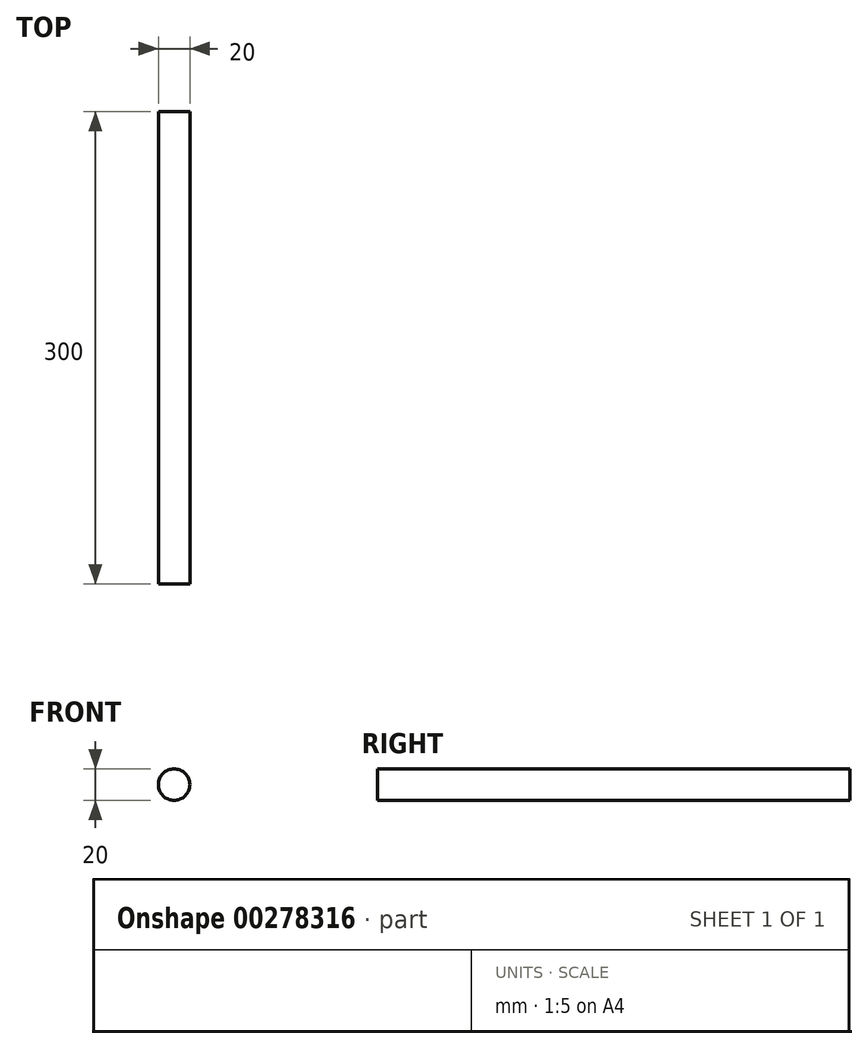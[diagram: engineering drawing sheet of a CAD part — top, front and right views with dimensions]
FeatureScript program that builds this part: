
annotation { "Feature Type Name" : "Feature", "Feature Type Description" : "" }
export const myFeature = defineFeature(function(context is Context, id is Id, definition is map)
    precondition{}
    {
        {
            var Q0;
            Q0=qCreatedBy(makeId("Front.planeOp"),FACE);
            var sketch = newSketch(context, id + "F0", { "sketchPlane" : qUnion([Q0])});
            skCircle(sketch, "E0", {"center": v(0, 0) * mm, "radius": 10 * mm});
            skSolve(sketch);
        }
        {
            var Q0;
            Q0=makeQuery(id+"F0.imprint","IMPRINT",FACE,{"disambiguationData":[TD([[makeQuery(id+"F0.imprint","IMPRINT",EDGE,{"derivedFrom":sQuery(id+"F0.wireOp",EDGE,"E0")}),1.0]])]});
            extrude(context, id + "F1", {"entities" : qUnion([Q0]), "endBound" : BoundingType.SYMMETRIC, "depth" : 300 * mm});
        }
    });
